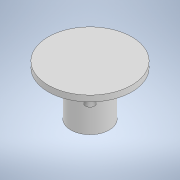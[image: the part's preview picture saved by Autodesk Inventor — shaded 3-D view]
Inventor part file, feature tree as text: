
AUTODESK INVENTOR PART (.ipt)
format: ipt  version: 2021 (Build 250183000, 183)  size: 126,976 bytes
history: native  units: mm
features: extrude x3, sketch x3, other x1
ambient origin geometry x8: Origin, YZ Plane, XZ Plane, XY Plane, X Axis, Y Axis, Z Axis, Center Point
bodies: Body1 (feature_tree)
feature tree (7):
  other  "Sólido1"
  extrude  "Extrusión1"  Depth=17.0mm
  extrude  "Extrusión2"  Depth=3.0mm
  extrude  "Extrusión3"  Depth=15.0mm
  sketch  "Boceto1"  dims[d0=17.0mm d1=17.0mm]
  sketch  "Boceto2"  dims[d2=3.0mm d3=3.0mm]
  sketch  "Boceto3"  dims[d4=3.0mm d5=3.0mm d6=2.0mm d7=0.0mm d8=4.0mm d9=0.0mm d10=13.0mm d11=15.0mm d12=0.0mm]
